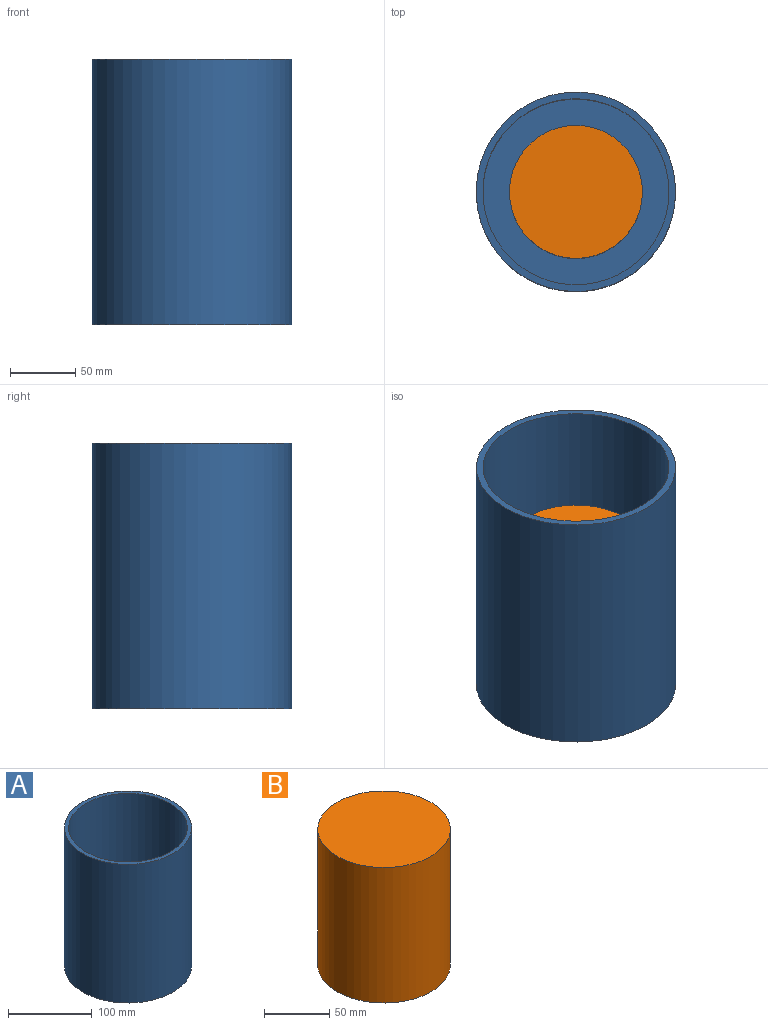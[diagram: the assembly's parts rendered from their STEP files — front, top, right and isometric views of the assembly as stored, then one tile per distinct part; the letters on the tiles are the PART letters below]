
ASSEMBLY  parts=2 mates=1
PART A: 5 faces, bbox 152.4x152.4x203.2 mm
  f0: cylinder r=76.2mm len=203.2mm, axis (0,0,-1), area 97287.8mm2, adj f1,f2
  f1: plane 152.4x152.4mm, normal (0,0,1), area 2351.1mm2, adj f0,f3
  f2: plane 152.4x152.4mm, normal (0,0,-1), area 18241.5mm2, adj f0
  f3: cylinder r=71.12mm len=198.12mm, axis (0,0,-1), area 88531.9mm2, adj f1,f4
  f4: plane 142.24x142.24mm, normal (0,0,1), area 15890.3mm2, adj f3
PART B: 3 faces, bbox 101.6x101.6x127 mm
  f0: cylinder r=50.8mm len=127mm, axis (0,0,-1), area 40536.6mm2, adj f1,f2
  f1: plane 101.6x101.6mm, normal (0,0,1), area 8107.3mm2, adj f0
  f2: plane 101.6x101.6mm, normal (0,0,-1), area 8107.3mm2, adj f0
PLACE A t=(-41.27,-28.18,30.39)mm
PLACE B rot(axis=(0,0,1),90deg) t=(-41.27,-28.18,35.47)mm
MATE revolute B.f0 <-> A.f0  axis (0,0,-1) through (-41.27,-28.18,86.27)mm
